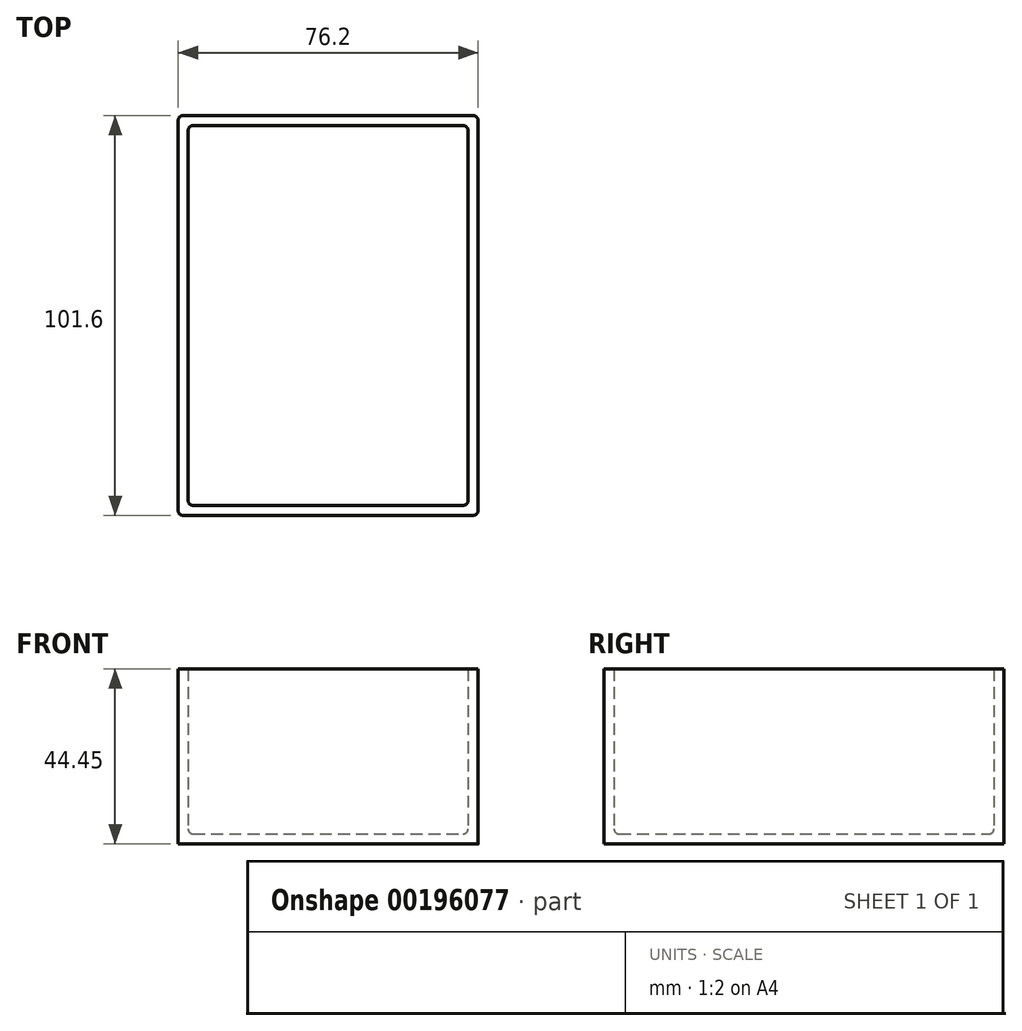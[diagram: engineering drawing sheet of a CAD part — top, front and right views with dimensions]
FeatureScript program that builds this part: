
annotation { "Feature Type Name" : "Feature", "Feature Type Description" : "" }
export const myFeature = defineFeature(function(context is Context, id is Id, definition is map)
    precondition{}
    {
        {
            var Q0;
            Q0=qCreatedBy(makeId("Top.planeOp"),FACE);
            var sketch = newSketch(context, id + "F0", { "sketchPlane" : qUnion([Q0])});
            skLineSegment(sketch, "E0.bottom", {"start": v(0, 0) * mm, "end": v(76.2, 0) * mm});
            skLineSegment(sketch, "E0.top", {"start": v(0, 101.6) * mm, "end": v(76.2, 101.6) * mm});
            skLineSegment(sketch, "E0.left", {"start": v(0, 0) * mm, "end": v(0, 101.6) * mm});
            skLineSegment(sketch, "E0.right", {"start": v(76.2, 0) * mm, "end": v(76.2, 101.6) * mm});
            skSolve(sketch);
        }
        {
            var Q0;
            Q0=makeQuery(id+"F0.imprint","IMPRINT",FACE,{"disambiguationData":[TD([[makeQuery(id+"F0.imprint","IMPRINT",EDGE,{"derivedFrom":sQuery(id+"F0.wireOp",EDGE,"E0.bottom")}),1.0]])]});
            extrude(context, id + "F1", {"entities" : qUnion([Q0]), "depth" : 44.45 * mm});
        }
        {
            var Q0;
            Q0=makeQuery(id+"F1.opExtrude","CAP_FACE",FACE,{"disambiguationData":[OSD([sQuery(id+"F0.wireOp",EDGE,"E0.bottom"),sQuery(id+"F0.wireOp",EDGE,"E0.top"),sQuery(id+"F0.wireOp",EDGE,"E0.left"),sQuery(id+"F0.wireOp",EDGE,"E0.right")])],"isStart":false});
            shell(context, id + "F2", {"entities" : qUnion([Q0]), "thickness" : 2.54 * mm});
        }
        {
            var Q0;
            Q0=makeQuery(id+"F2.opShell","OFFSET_EDGE",EDGE,{"disambiguationData":[OSD([sQuery(id+"F0.wireOp",EDGE,"E0.bottom"),sQuery(id+"F0.wireOp",EDGE,"E0.left")])]});
            var Q1;
            Q1=makeQuery(id+"F2.opShell","OFFSET_EDGE",EDGE,{"disambiguationData":[OSD([sQuery(id+"F0.wireOp",EDGE,"E0.top"),sQuery(id+"F0.wireOp",EDGE,"E0.left")])]});
            var Q2;
            Q2=makeQuery(id+"F2.opShell","OFFSET_EDGE",EDGE,{"disambiguationData":[OSD([sQuery(id+"F0.wireOp",EDGE,"E0.bottom"),sQuery(id+"F0.wireOp",EDGE,"E0.right")])]});
            var Q3;
            Q3=makeQuery(id+"F2.opShell","OFFSET_EDGE",EDGE,{"disambiguationData":[OSD([sQuery(id+"F0.wireOp",EDGE,"E0.top"),sQuery(id+"F0.wireOp",EDGE,"E0.right")])]});
            var Q4;
            Q4=makeQuery(id+"F1.opExtrude","SWEPT_EDGE",EDGE,{"disambiguationData":[OSD([sQuery(id+"F0.wireOp",EDGE,"E0.bottom"),sQuery(id+"F0.wireOp",EDGE,"E0.left")])]});
            var Q5;
            Q5=makeQuery(id+"F1.opExtrude","SWEPT_EDGE",EDGE,{"disambiguationData":[OSD([sQuery(id+"F0.wireOp",EDGE,"E0.top"),sQuery(id+"F0.wireOp",EDGE,"E0.left")])]});
            var Q6;
            Q6=makeQuery(id+"F1.opExtrude","SWEPT_EDGE",EDGE,{"disambiguationData":[OSD([sQuery(id+"F0.wireOp",EDGE,"E0.bottom"),sQuery(id+"F0.wireOp",EDGE,"E0.right")])]});
            var Q7;
            Q7=makeQuery(id+"F1.opExtrude","SWEPT_EDGE",EDGE,{"disambiguationData":[OSD([sQuery(id+"F0.wireOp",EDGE,"E0.top"),sQuery(id+"F0.wireOp",EDGE,"E0.right")])]});
            fillet(context, id + "F3", {"entities" : qUnion([Q0, Q1, Q2, Q3, Q4, Q5, Q6, Q7]), "radius" : 1.27 * mm, "tangentPropagation" : true, "allowEdgeOverflow" : false});
        }
        {
            var Q0;
            Q0=makeQuery(id+"F2.opShell","OFFSET_FACE",FACE,{"disambiguationData":[OSD([sQuery(id+"F0.wireOp",EDGE,"E0.bottom"),sQuery(id+"F0.wireOp",EDGE,"E0.top"),sQuery(id+"F0.wireOp",EDGE,"E0.left"),sQuery(id+"F0.wireOp",EDGE,"E0.right")])]});
            fillet(context, id + "F4", {"entities" : qUnion([Q0]), "radius" : 1.27 * mm, "tangentPropagation" : true, "allowEdgeOverflow" : false});
        }
    });
